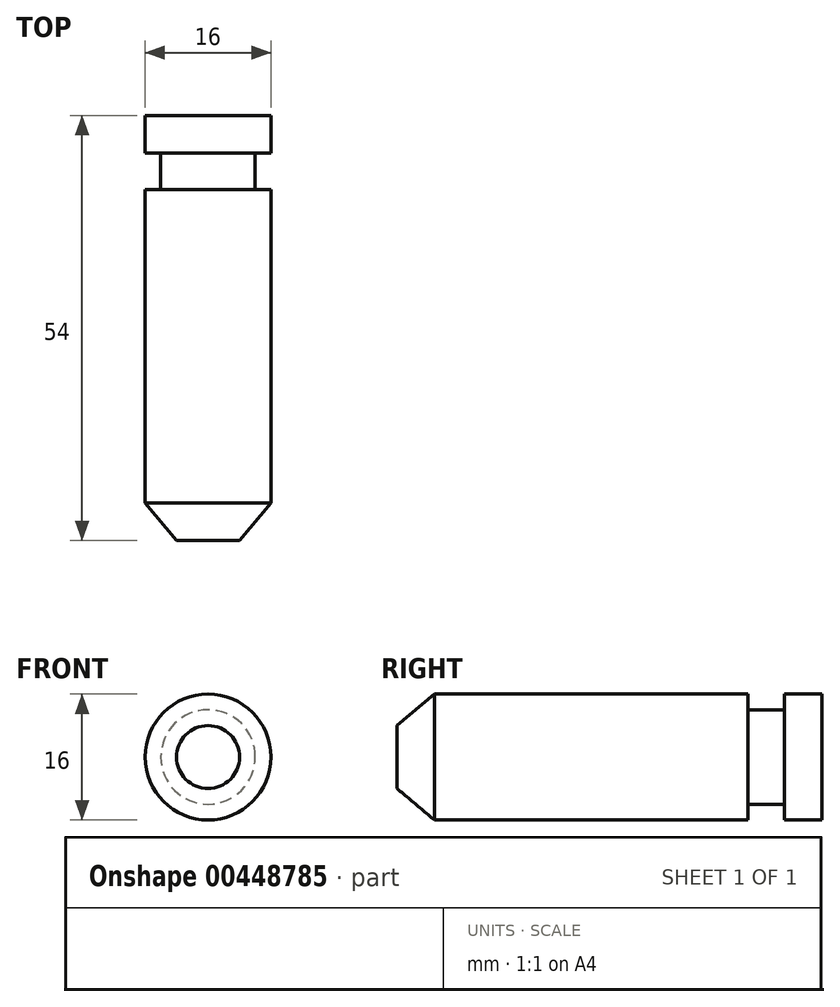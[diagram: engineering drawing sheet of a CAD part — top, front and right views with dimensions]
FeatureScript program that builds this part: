
annotation { "Feature Type Name" : "Feature", "Feature Type Description" : "" }
export const myFeature = defineFeature(function(context is Context, id is Id, definition is map)
    precondition{}
    {
        {
            var Q0;
            Q0=qCreatedBy(makeId("Top.planeOp"),FACE);
            var sketch = newSketch(context, id + "F0", { "sketchPlane" : qUnion([Q0])});
            skLineSegment(sketch, "E0", {"start": v(0, 54) * mm, "end": v(-8, 54) * mm});
            skLineSegment(sketch, "E1", {"start": v(-8, 54) * mm, "end": v(-8, 49.2) * mm});
            skLineSegment(sketch, "E2", {"start": v(-8, 49.2) * mm, "end": v(-6, 49.2) * mm});
            skLineSegment(sketch, "E3", {"start": v(-6, 49.2) * mm, "end": v(-6, 44.6) * mm});
            skLineSegment(sketch, "E4", {"start": v(-6, 44.6) * mm, "end": v(-8, 44.6) * mm});
            skLineSegment(sketch, "E5", {"start": v(-8, 44.6) * mm, "end": v(-8, 4.77) * mm});
            skLineSegment(sketch, "E6", {"start": v(-8, 4.77) * mm, "end": v(-4, 0) * mm});
            skLineSegment(sketch, "E7", {"start": v(-4, 0) * mm, "end": v(0, 0) * mm});
            skLineSegment(sketch, "E8", {"start": v(0, 0) * mm, "end": v(0, 54) * mm});
            skSolve(sketch);
        }
        {
            var Q0;
            Q0=makeQuery(id+"F0.imprint","IMPRINT",FACE,{"disambiguationData":[TD([[makeQuery(id+"F0.imprint","IMPRINT",EDGE,{"derivedFrom":sQuery(id+"F0.wireOp",EDGE,"E0")}),1.0]])]});
            var Q1;
            Q1=sQuery(id+"F0.wireOp",EDGE,"E8");
            revolve(context, id + "F1", {"entities" : qUnion([Q0]), "axis" : qUnion([Q1]), "revolveType" : RevolveType.FULL});
        }
    });
